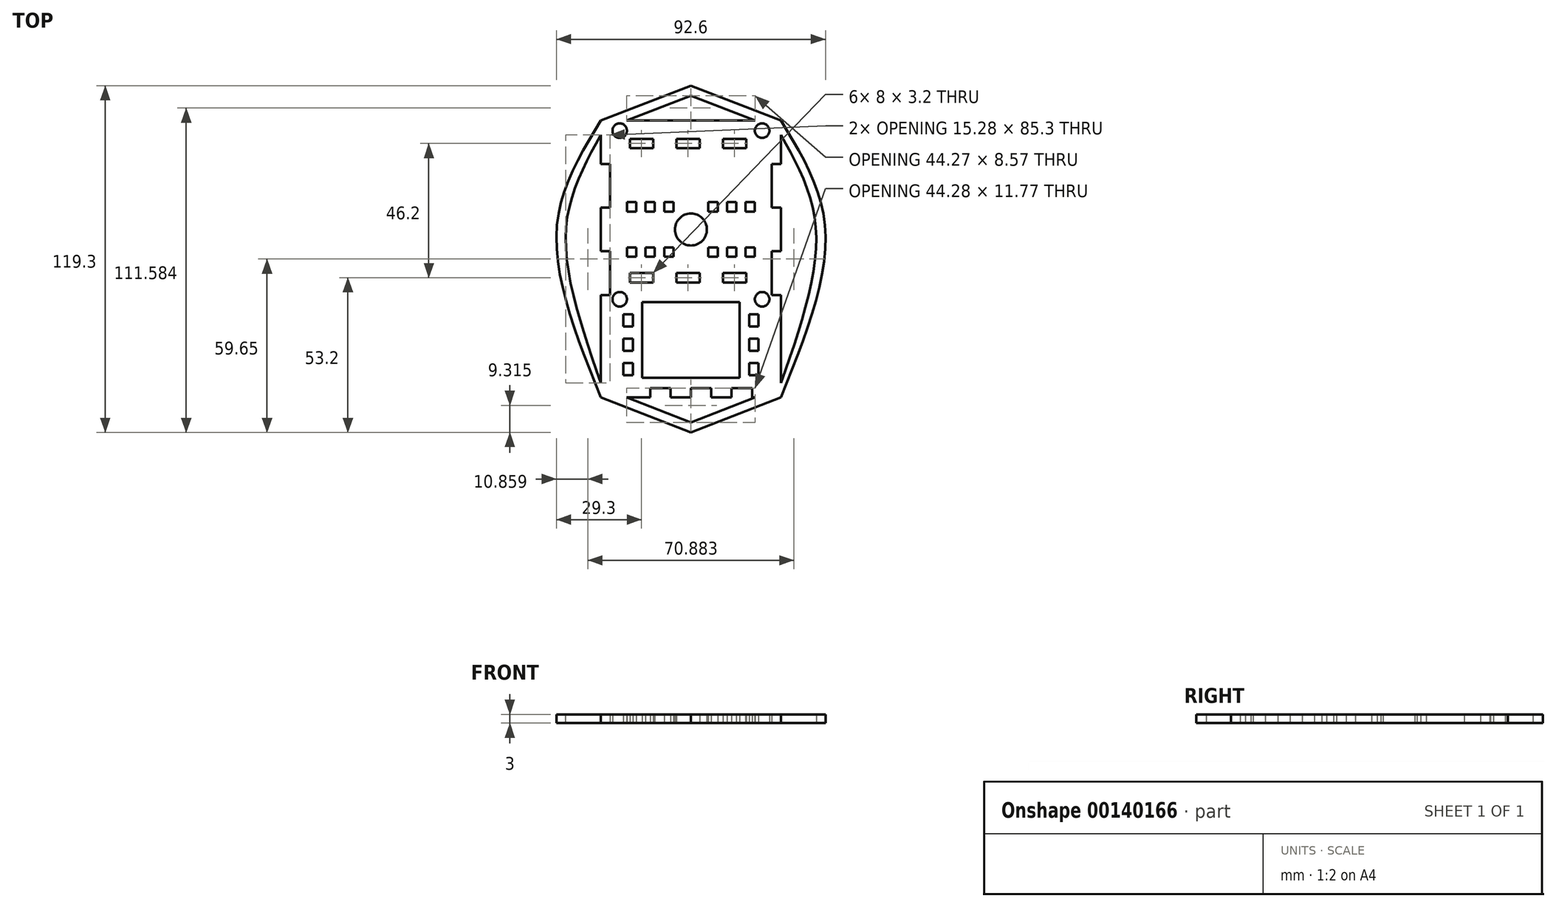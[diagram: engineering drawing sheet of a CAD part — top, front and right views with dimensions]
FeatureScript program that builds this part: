
annotation { "Feature Type Name" : "Feature", "Feature Type Description" : "" }
export const myFeature = defineFeature(function(context is Context, id is Id, definition is map)
    precondition{}
    {
        {
            var Q0;
            Q0=qCreatedBy(makeId("Top.planeOp"),FACE);
            var sketch = newSketch(context, id + "F0", { "sketchPlane" : qUnion([Q0])});
            skLineSegment(sketch, "E0.top", {"start": v(0, 37.5) * mm, "end": v(-22.14, 37.5) * mm});
            skLineSegment(sketch, "E0.right", {"start": v(-31, -32.5) * mm, "end": v(-31, -22.5) * mm});
            skPoint(sketch, "E0.middle", {"position": v(0, 0) * mm});
            skLineSegment(sketch, "E1", {"start": v(-31, 22.5) * mm, "end": v(-27.8, 22.5) * mm});
            skLineSegment(sketch, "E2", {"start": v(-27.8, 22.5) * mm, "end": v(-27.8, 7.5) * mm});
            skLineSegment(sketch, "E3", {"start": v(-27.8, 7.5) * mm, "end": v(-31, 7.5) * mm});
            skLineSegment(sketch, "E4", {"start": v(-31, 7.5) * mm, "end": v(-31, -7.5) * mm});
            skLineSegment(sketch, "E5", {"start": v(-31, -7.5) * mm, "end": v(-27.8, -7.5) * mm});
            skLineSegment(sketch, "E6", {"start": v(-27.8, -7.5) * mm, "end": v(-27.8, -22.5) * mm});
            skLineSegment(sketch, "E7", {"start": v(-27.8, -22.5) * mm, "end": v(-31, -22.5) * mm});
            skLineSegment(sketch, "E8", {"start": v(-31, -22.5) * mm, "end": v(-31, -32.5) * mm});
            skLineSegment(sketch, "E9", {"start": v(27.8, 22.5) * mm, "end": v(31, 22.5) * mm});
            skLineSegment(sketch, "E10", {"start": v(31, 7.5) * mm, "end": v(27.8, 7.5) * mm});
            skLineSegment(sketch, "E11", {"start": v(27.8, -7.5) * mm, "end": v(31, -7.5) * mm});
            skLineSegment(sketch, "E12", {"start": v(31, -22.5) * mm, "end": v(27.8, -22.5) * mm});
            skLineSegment(sketch, "E13.trimOffspring", {"start": v(-31, 22.5) * mm, "end": v(-31, 32.5) * mm});
            skLineSegment(sketch, "E14.trimOffspring", {"start": v(-31, -7.5) * mm, "end": v(-31, 7.5) * mm});
            skCircle(sketch, "E15", {"center": v(0, 0) * mm, "radius": 5.5 * mm});
            skLineSegment(sketch, "E16", {"start": v(0, 0) * mm, "end": v(5.5, 0) * mm, "construction": true});
            skLineSegment(sketch, "E17", {"start": v(-31, 0) * mm, "end": v(0, 0) * mm, "construction": true});
            skLineSegment(sketch, "E18", {"start": v(0, -14.47) * mm, "end": v(0, 12.75) * mm, "construction": true});
            skLineSegment(sketch, "E19", {"start": v(5.5, 0) * mm, "end": v(6, 0) * mm, "construction": true});
            skLineSegment(sketch, "E20", {"start": v(6, 0) * mm, "end": v(6, 9.4) * mm, "construction": true});
            skLineSegment(sketch, "E21.bottom", {"start": v(6, 9.4) * mm, "end": v(9.2, 9.4) * mm});
            skLineSegment(sketch, "E21.top", {"start": v(6, 6.2) * mm, "end": v(9.2, 6.2) * mm});
            skLineSegment(sketch, "E21.left", {"start": v(6, 9.4) * mm, "end": v(6, 6.2) * mm});
            skLineSegment(sketch, "E21.right", {"start": v(9.2, 9.4) * mm, "end": v(9.2, 6.2) * mm});
            skLineSegment(sketch, "E22", {"start": v(6, 0) * mm, "end": v(12.4, 0) * mm, "construction": true});
            skLineSegment(sketch, "E23", {"start": v(12.4, 0) * mm, "end": v(12.4, 9.4) * mm, "construction": true});
            skLineSegment(sketch, "E24", {"start": v(12.4, 0) * mm, "end": v(18.8, 0) * mm, "construction": true});
            skLineSegment(sketch, "E25", {"start": v(18.8, 0) * mm, "end": v(18.8, 9.4) * mm, "construction": true});
            skLineSegment(sketch, "E26", {"start": v(18.8, 0) * mm, "end": v(24, 0) * mm, "construction": true});
            skLineSegment(sketch, "E27.bottom", {"start": v(12.4, 9.4) * mm, "end": v(15.6, 9.4) * mm});
            skLineSegment(sketch, "E27.top", {"start": v(12.4, 6.2) * mm, "end": v(15.6, 6.2) * mm});
            skLineSegment(sketch, "E27.left", {"start": v(12.4, 9.4) * mm, "end": v(12.4, 6.2) * mm});
            skLineSegment(sketch, "E27.right", {"start": v(15.6, 9.4) * mm, "end": v(15.6, 6.2) * mm});
            skLineSegment(sketch, "E28.bottom", {"start": v(18.8, 9.4) * mm, "end": v(22, 9.4) * mm});
            skLineSegment(sketch, "E28.top", {"start": v(18.8, 6.2) * mm, "end": v(22, 6.2) * mm});
            skLineSegment(sketch, "E28.left", {"start": v(18.8, 9.4) * mm, "end": v(18.8, 6.2) * mm});
            skLineSegment(sketch, "E28.right", {"start": v(22, 9.4) * mm, "end": v(22, 6.2) * mm});
            skLineSegment(sketch, "E29.MirrorCS", {"start": v(-5.5, 0) * mm, "end": v(-6, 0) * mm, "construction": true});
            skLineSegment(sketch, "E30.MirrorCS", {"start": v(-6, 0) * mm, "end": v(-12.4, 0) * mm, "construction": true});
            skLineSegment(sketch, "E31.MirrorCS", {"start": v(-18.8, 0) * mm, "end": v(-24, 0) * mm, "construction": true});
            skLineSegment(sketch, "E32.MirrorCS", {"start": v(-12.4, 0) * mm, "end": v(-18.8, 0) * mm, "construction": true});
            skLineSegment(sketch, "E33", {"start": v(-31, 0) * mm, "end": v(27.8, 0) * mm, "construction": true});
            skLineSegment(sketch, "E34.MirrorCS", {"start": v(0, 0) * mm, "end": v(0, 30) * mm, "construction": true});
            skLineSegment(sketch, "E35.MirrorCS", {"start": v(6, -9.4) * mm, "end": v(9.2, -9.4) * mm});
            skLineSegment(sketch, "E36.MirrorCS", {"start": v(12.4, -9.4) * mm, "end": v(12.4, -6.2) * mm});
            skLineSegment(sketch, "E37.MirrorCS", {"start": v(18.8, -9.4) * mm, "end": v(18.8, -6.2) * mm});
            skLineSegment(sketch, "E38.MirrorCS", {"start": v(6, -9.4) * mm, "end": v(6, -6.2) * mm});
            skLineSegment(sketch, "E39.MirrorCS", {"start": v(18.8, -9.4) * mm, "end": v(22, -9.4) * mm});
            skLineSegment(sketch, "E40.MirrorCS", {"start": v(6, -6.2) * mm, "end": v(9.2, -6.2) * mm});
            skLineSegment(sketch, "E41.MirrorCS", {"start": v(12.4, 0) * mm, "end": v(12.4, -9.4) * mm, "construction": true});
            skLineSegment(sketch, "E42.MirrorCS", {"start": v(9.2, -9.4) * mm, "end": v(9.2, -6.2) * mm});
            skLineSegment(sketch, "E43.MirrorCS", {"start": v(15.6, -9.4) * mm, "end": v(15.6, -6.2) * mm});
            skLineSegment(sketch, "E44.MirrorCS", {"start": v(12.4, -6.2) * mm, "end": v(15.6, -6.2) * mm});
            skLineSegment(sketch, "E45.MirrorCS", {"start": v(12.4, -9.4) * mm, "end": v(15.6, -9.4) * mm});
            skLineSegment(sketch, "E46.MirrorCS", {"start": v(18.8, 0) * mm, "end": v(18.8, -9.4) * mm, "construction": true});
            skLineSegment(sketch, "E47.MirrorCS", {"start": v(18.8, -6.2) * mm, "end": v(22, -6.2) * mm});
            skLineSegment(sketch, "E48.MirrorCS", {"start": v(22, -9.4) * mm, "end": v(22, -6.2) * mm});
            skLineSegment(sketch, "E49.MirrorCS", {"start": v(6, 0) * mm, "end": v(6, -9.4) * mm, "construction": true});
            skLineSegment(sketch, "E50.MirrorCS", {"start": v(-9.2, 9.4) * mm, "end": v(-9.2, 6.2) * mm});
            skLineSegment(sketch, "E51.MirrorCS", {"start": v(-15.6, 9.4) * mm, "end": v(-15.6, 6.2) * mm});
            skLineSegment(sketch, "E52.MirrorCS", {"start": v(-12.4, 9.4) * mm, "end": v(-15.6, 9.4) * mm});
            skLineSegment(sketch, "E53.MirrorCS", {"start": v(-18.8, 6.2) * mm, "end": v(-22, 6.2) * mm});
            skLineSegment(sketch, "E54.MirrorCS", {"start": v(-18.8, 9.4) * mm, "end": v(-18.8, 6.2) * mm});
            skLineSegment(sketch, "E55.MirrorCS", {"start": v(-6, 9.4) * mm, "end": v(-9.2, 9.4) * mm});
            skLineSegment(sketch, "E56.MirrorCS", {"start": v(-22, 9.4) * mm, "end": v(-22, 6.2) * mm});
            skLineSegment(sketch, "E57.MirrorCS", {"start": v(-18.8, 9.4) * mm, "end": v(-22, 9.4) * mm});
            skLineSegment(sketch, "E58.MirrorCS", {"start": v(-6, 6.2) * mm, "end": v(-9.2, 6.2) * mm});
            skLineSegment(sketch, "E59.MirrorCS", {"start": v(-12.4, 9.4) * mm, "end": v(-12.4, 6.2) * mm});
            skLineSegment(sketch, "E60.MirrorCS", {"start": v(-12.4, 6.2) * mm, "end": v(-15.6, 6.2) * mm});
            skLineSegment(sketch, "E61.MirrorCS", {"start": v(-6, 9.4) * mm, "end": v(-6, 6.2) * mm});
            skLineSegment(sketch, "E62.MirrorCS", {"start": v(-18.8, -9.4) * mm, "end": v(-18.8, -6.2) * mm});
            skLineSegment(sketch, "E63.MirrorCS", {"start": v(-12.4, -9.4) * mm, "end": v(-12.4, -6.2) * mm});
            skLineSegment(sketch, "E64.MirrorCS", {"start": v(-6, -9.4) * mm, "end": v(-6, -6.2) * mm});
            skLineSegment(sketch, "E65.MirrorCS", {"start": v(-12.4, -9.4) * mm, "end": v(-15.6, -9.4) * mm});
            skLineSegment(sketch, "E66.MirrorCS", {"start": v(-18.8, -6.2) * mm, "end": v(-22, -6.2) * mm});
            skLineSegment(sketch, "E67.MirrorCS", {"start": v(-18.8, -9.4) * mm, "end": v(-22, -9.4) * mm});
            skLineSegment(sketch, "E68.MirrorCS", {"start": v(-12.4, -6.2) * mm, "end": v(-15.6, -6.2) * mm});
            skLineSegment(sketch, "E69.MirrorCS", {"start": v(-12.4, 0) * mm, "end": v(-12.4, -9.4) * mm, "construction": true});
            skLineSegment(sketch, "E70.MirrorCS", {"start": v(-18.8, 0) * mm, "end": v(-18.8, -9.4) * mm, "construction": true});
            skLineSegment(sketch, "E71.MirrorCS", {"start": v(-6, -9.4) * mm, "end": v(-9.2, -9.4) * mm});
            skLineSegment(sketch, "E72.MirrorCS", {"start": v(-6, 0) * mm, "end": v(-6, -9.4) * mm, "construction": true});
            skLineSegment(sketch, "E73.MirrorCS", {"start": v(-22, -9.4) * mm, "end": v(-22, -6.2) * mm});
            skLineSegment(sketch, "E74.MirrorCS", {"start": v(-9.2, -9.4) * mm, "end": v(-9.2, -6.2) * mm});
            skLineSegment(sketch, "E75.MirrorCS", {"start": v(-6, -6.2) * mm, "end": v(-9.2, -6.2) * mm});
            skLineSegment(sketch, "E76.MirrorCS", {"start": v(-15.6, -9.4) * mm, "end": v(-15.6, -6.2) * mm});
            skLineSegment(sketch, "E77", {"start": v(31, 32.5) * mm, "end": v(31, 22.5) * mm});
            skLineSegment(sketch, "E78", {"start": v(27.8, 22.5) * mm, "end": v(27.8, 7.5) * mm});
            skLineSegment(sketch, "E79", {"start": v(27.8, -7.5) * mm, "end": v(27.8, -22.5) * mm});
            skLineSegment(sketch, "E80.trimOffspring", {"start": v(31, -22.5) * mm, "end": v(31, -32.5) * mm});
            skLineSegment(sketch, "E81", {"start": v(31, 7.5) * mm, "end": v(31, -7.5) * mm});
            skLineSegment(sketch, "E82", {"start": v(31, 22.5) * mm, "end": v(34.2, 22.5) * mm});
            skLineSegment(sketch, "E83", {"start": v(0, 37.5) * mm, "end": v(0, 49.5) * mm, "construction": true});
            skPoint(sketch, "E83.startSnap0", {"position": v(0, 15) * mm});
            skLineSegment(sketch, "E84", {"start": v(0, 43.5) * mm, "end": v(34.2, 43.5) * mm, "construction": true});
            skLineSegment(sketch, "E85", {"start": v(0, 43.5) * mm, "end": v(-40.16, 43.5) * mm, "construction": true});
            skLineSegment(sketch, "E86", {"start": v(34.2, 37.5) * mm, "end": v(34.2, 43.5) * mm, "construction": true});
            skLineSegment(sketch, "E87", {"start": v(-31, 0) * mm, "end": v(-43, 0) * mm, "construction": true});
            skLineSegment(sketch, "E88", {"start": v(-27.8, 15) * mm, "end": v(-54.38, 15) * mm, "construction": true});
            skLineSegment(sketch, "E89", {"start": v(-27.8, -15) * mm, "end": v(-55.02, -15) * mm, "construction": true});
            skLineSegment(sketch, "E90", {"start": v(-31, 0) * mm, "end": v(-31, -20) * mm, "construction": true});
            skLineSegment(sketch, "E91", {"start": v(-31, 0) * mm, "end": v(-31, 20) * mm, "construction": true});
            skLineSegment(sketch, "E92", {"start": v(-31, 20) * mm, "end": v(-43, 20) * mm, "construction": true});
            skLineSegment(sketch, "E93", {"start": v(-43, 20) * mm, "end": v(-43, -20) * mm, "construction": true});
            skLineSegment(sketch, "E94", {"start": v(-31, -32.5) * mm, "end": v(-31, -28.4) * mm, "construction": true});
            skLineSegment(sketch, "E95", {"start": v(-31, 37.5) * mm, "end": v(0, 49.5) * mm});
            skLineSegment(sketch, "E96", {"start": v(0, 49.5) * mm, "end": v(31, 37.5) * mm});
            skLineSegment(sketch, "E97", {"start": v(0, 49.5) * mm, "end": v(0, 46.3) * mm, "construction": true});
            skLineSegment(sketch, "E98", {"start": v(0, 46.07) * mm, "end": v(-22.14, 37.5) * mm, "construction": true});
            skLineSegment(sketch, "E99.MirrorCS", {"start": v(0, 46.07) * mm, "end": v(22.14, 37.5) * mm, "construction": true});
            skLineSegment(sketch, "E100", {"start": v(0, 46.07) * mm, "end": v(22.14, 37.5) * mm});
            skLineSegment(sketch, "E101", {"start": v(0, 46.07) * mm, "end": v(-22.14, 37.5) * mm});
            skPoint(sketch, "E102.orphan", {"position": v(27.8, 37.5) * mm});
            skLineSegment(sketch, "E103", {"start": v(0, 37.5) * mm, "end": v(22.14, 37.5) * mm});
            skPoint(sketch, "E0.left.start.orphan", {"position": v(31, -37.5) * mm});
            skLineSegment(sketch, "E104", {"start": v(-43, 0) * mm, "end": v(-46.2, 0) * mm, "construction": true});
            skLineSegment(sketch, "E105", {"start": v(-31, 37.5) * mm, "end": v(31, 37.5) * mm, "construction": true});
            skLineSegment(sketch, "E106", {"start": v(-31, 37.5) * mm, "end": v(-31, 34.3) * mm, "construction": true});
            skLineSegment(sketch, "E107", {"start": v(-31, 34) * mm, "end": v(31, 34) * mm, "construction": true});
            skLineSegment(sketch, "E108", {"start": v(0, 34) * mm, "end": v(-24.5, 34) * mm, "construction": true});
            skLineSegment(sketch, "E109", {"start": v(-24.5, 34) * mm, "end": v(-24.5, -24) * mm, "construction": true});
            skLineSegment(sketch, "E110", {"start": v(24.5, 34) * mm, "end": v(24.5, -24) * mm, "construction": true});
            skLineSegment(sketch, "E111.MirrorCS", {"start": v(-13, 28) * mm, "end": v(-21, 28) * mm});
            skLineSegment(sketch, "E112.MirrorCS", {"start": v(-13, 28) * mm, "end": v(-5, 28) * mm, "construction": true});
            skLineSegment(sketch, "E113.MirrorCS", {"start": v(-5, 28) * mm, "end": v(-5, 31.2) * mm});
            skLineSegment(sketch, "E114.MirrorCS", {"start": v(3, 28) * mm, "end": v(-5, 28) * mm});
            skLineSegment(sketch, "E115.MirrorCS", {"start": v(3, 28) * mm, "end": v(11, 28) * mm, "construction": true});
            skLineSegment(sketch, "E116.MirrorCS", {"start": v(19, 28) * mm, "end": v(11, 28) * mm});
            skLineSegment(sketch, "E117.MirrorCS", {"start": v(-21, 28) * mm, "end": v(-21, 31.2) * mm});
            skLineSegment(sketch, "E118.MirrorCS", {"start": v(-13, 31.2) * mm, "end": v(-13, 28) * mm});
            skLineSegment(sketch, "E119.MirrorCS", {"start": v(-5, 31.2) * mm, "end": v(3, 31.2) * mm});
            skLineSegment(sketch, "E120.MirrorCS", {"start": v(3, 31.2) * mm, "end": v(3, 28) * mm});
            skLineSegment(sketch, "E121.MirrorCS", {"start": v(11, 28) * mm, "end": v(11, 31.2) * mm});
            skLineSegment(sketch, "E122.MirrorCS", {"start": v(19, 31.2) * mm, "end": v(19, 28) * mm});
            skLineSegment(sketch, "E123.MirrorCS", {"start": v(11, 31.2) * mm, "end": v(19, 31.2) * mm});
            skLineSegment(sketch, "E124.MirrorCS", {"start": v(0, 28) * mm, "end": v(21, 28) * mm, "construction": true});
            skLineSegment(sketch, "E125.MirrorCS", {"start": v(0, 28) * mm, "end": v(-21, 28) * mm, "construction": true});
            skLineSegment(sketch, "E126.MirrorCS", {"start": v(-21, 31.2) * mm, "end": v(-13, 31.2) * mm});
            skLineSegment(sketch, "E127.trimOffspring", {"start": v(-31, 32.5) * mm, "end": v(-31, 22.5) * mm});
            skLineSegment(sketch, "E128", {"start": v(43, 0) * mm, "end": v(46.2, 0) * mm, "construction": true});
            skLineSegment(sketch, "E129", {"start": v(-27.8, -15) * mm, "end": v(27.8, -15) * mm, "construction": true});
            skLineSegment(sketch, "E130", {"start": v(0, -23.1) * mm, "end": v(-21.89, -23.1) * mm, "construction": true});
            skLineSegment(sketch, "E131", {"start": v(0, -23.1) * mm, "end": v(22.57, -23.1) * mm, "construction": true});
            skLineSegment(sketch, "E132.MirrorCS", {"start": v(-13, -18.2) * mm, "end": v(-21, -18.2) * mm});
            skLineSegment(sketch, "E133.MirrorCS", {"start": v(-21, -18.2) * mm, "end": v(-21, -15) * mm});
            skLineSegment(sketch, "E134.MirrorCS", {"start": v(-21, -15) * mm, "end": v(-13, -15) * mm});
            skLineSegment(sketch, "E135.MirrorCS", {"start": v(-13, -15) * mm, "end": v(-13, -18.2) * mm});
            skLineSegment(sketch, "E136.MirrorCS", {"start": v(-13, -18.2) * mm, "end": v(-5, -18.2) * mm, "construction": true});
            skLineSegment(sketch, "E137.MirrorCS", {"start": v(-5, -18.2) * mm, "end": v(-5, -15) * mm});
            skLineSegment(sketch, "E138.MirrorCS", {"start": v(-5, -15) * mm, "end": v(3, -15) * mm});
            skLineSegment(sketch, "E139.MirrorCS", {"start": v(3, -15) * mm, "end": v(3, -18.2) * mm});
            skLineSegment(sketch, "E140.MirrorCS", {"start": v(3, -18.2) * mm, "end": v(-5, -18.2) * mm});
            skLineSegment(sketch, "E141.MirrorCS", {"start": v(0, -18.2) * mm, "end": v(-21, -18.2) * mm, "construction": true});
            skLineSegment(sketch, "E142.MirrorCS", {"start": v(11, -18.2) * mm, "end": v(11, -15) * mm});
            skLineSegment(sketch, "E143.MirrorCS", {"start": v(19, -18.2) * mm, "end": v(11, -18.2) * mm});
            skLineSegment(sketch, "E144.MirrorCS", {"start": v(19, -15) * mm, "end": v(19, -18.2) * mm});
            skLineSegment(sketch, "E145.MirrorCS", {"start": v(11, -15) * mm, "end": v(19, -15) * mm});
            skCircle(sketch, "E146", {"center": v(24.5, -24) * mm, "radius": 2.5 * mm});
            skCircle(sketch, "E147", {"center": v(-24.5, -24) * mm, "radius": 2.5 * mm});
            skCircle(sketch, "E148", {"center": v(-24.5, 34) * mm, "radius": 2.5 * mm});
            skCircle(sketch, "E149", {"center": v(24.5, 34) * mm, "radius": 2.5 * mm});
            skLineSegment(sketch, "E150", {"start": v(-31, -28.4) * mm, "end": v(31, -28.4) * mm, "construction": true});
            skLineSegment(sketch, "E151", {"start": v(0, -28.4) * mm, "end": v(0, -57.8) * mm, "construction": true});
            skLineSegment(sketch, "E152", {"start": v(0, -28.4) * mm, "end": v(-25, -28.4) * mm, "construction": true});
            skLineSegment(sketch, "E153", {"start": v(-25, -28.4) * mm, "end": v(-25, -57.8) * mm, "construction": true});
            skLineSegment(sketch, "E154", {"start": v(0, -28.4) * mm, "end": v(25, -28.4) * mm, "construction": true});
            skLineSegment(sketch, "E155", {"start": v(25, -28.4) * mm, "end": v(25, -57.8) * mm, "construction": true});
            skLineSegment(sketch, "E156", {"start": v(22.14, -57.8) * mm, "end": v(21, -57.8) * mm, "construction": true});
            skLineSegment(sketch, "E157", {"start": v(25, -28.4) * mm, "end": v(20, -28.4) * mm, "construction": true});
            skLineSegment(sketch, "E158", {"start": v(20, -28.4) * mm, "end": v(20, -57.8) * mm, "construction": true});
            skLineSegment(sketch, "E159", {"start": v(20, -28.4) * mm, "end": v(20, -29.13) * mm, "construction": true});
            skLineSegment(sketch, "E160", {"start": v(20, -29.13) * mm, "end": v(23.2, -29.13) * mm});
            skLineSegment(sketch, "E161", {"start": v(23.2, -29.13) * mm, "end": v(23.2, -33.33) * mm});
            skLineSegment(sketch, "E162", {"start": v(23.2, -33.33) * mm, "end": v(20, -33.33) * mm});
            skLineSegment(sketch, "E163", {"start": v(20, -33.33) * mm, "end": v(20, -29.13) * mm});
            skLineSegment(sketch, "E164", {"start": v(20, -33.33) * mm, "end": v(20, -37.53) * mm, "construction": true});
            skLineSegment(sketch, "E165", {"start": v(20, -37.53) * mm, "end": v(23.2, -37.53) * mm});
            skLineSegment(sketch, "E166", {"start": v(23.2, -37.53) * mm, "end": v(23.2, -41.73) * mm});
            skLineSegment(sketch, "E167", {"start": v(23.2, -41.73) * mm, "end": v(20, -41.73) * mm});
            skLineSegment(sketch, "E168", {"start": v(20, -41.73) * mm, "end": v(20, -37.53) * mm});
            skLineSegment(sketch, "E169", {"start": v(20, -41.73) * mm, "end": v(20, -45.93) * mm, "construction": true});
            skLineSegment(sketch, "E170", {"start": v(20, -45.93) * mm, "end": v(23.2, -45.93) * mm});
            skLineSegment(sketch, "E171", {"start": v(23.2, -45.93) * mm, "end": v(23.2, -50.13) * mm});
            skLineSegment(sketch, "E172", {"start": v(23.2, -50.13) * mm, "end": v(20, -50.13) * mm});
            skLineSegment(sketch, "E173", {"start": v(20, -50.13) * mm, "end": v(20, -45.93) * mm});
            skLineSegment(sketch, "E174.MirrorCS", {"start": v(-20, -28.4) * mm, "end": v(-20, -29.13) * mm, "construction": true});
            skLineSegment(sketch, "E175.MirrorCS", {"start": v(-20, -33.33) * mm, "end": v(-20, -29.13) * mm});
            skLineSegment(sketch, "E176.MirrorCS", {"start": v(-23.2, -29.13) * mm, "end": v(-23.2, -33.33) * mm});
            skLineSegment(sketch, "E177.MirrorCS", {"start": v(-20, -29.13) * mm, "end": v(-23.2, -29.13) * mm});
            skLineSegment(sketch, "E178.MirrorCS", {"start": v(-23.2, -50.13) * mm, "end": v(-20, -50.13) * mm});
            skLineSegment(sketch, "E179.MirrorCS", {"start": v(-20, -50.13) * mm, "end": v(-20, -45.93) * mm});
            skLineSegment(sketch, "E180.MirrorCS", {"start": v(-23.2, -45.93) * mm, "end": v(-23.2, -50.13) * mm});
            skLineSegment(sketch, "E181.MirrorCS", {"start": v(-20, -45.93) * mm, "end": v(-23.2, -45.93) * mm});
            skLineSegment(sketch, "E182.MirrorCS", {"start": v(-20, -41.73) * mm, "end": v(-20, -45.93) * mm, "construction": true});
            skLineSegment(sketch, "E183.MirrorCS", {"start": v(-20, -41.73) * mm, "end": v(-20, -37.53) * mm});
            skLineSegment(sketch, "E184.MirrorCS", {"start": v(-23.2, -41.73) * mm, "end": v(-20, -41.73) * mm});
            skLineSegment(sketch, "E185.MirrorCS", {"start": v(-23.2, -37.53) * mm, "end": v(-23.2, -41.73) * mm});
            skLineSegment(sketch, "E186.MirrorCS", {"start": v(-20, -37.53) * mm, "end": v(-23.2, -37.53) * mm});
            skLineSegment(sketch, "E187.MirrorCS", {"start": v(-20, -33.33) * mm, "end": v(-20, -37.53) * mm, "construction": true});
            skLineSegment(sketch, "E188.MirrorCS", {"start": v(-23.2, -33.33) * mm, "end": v(-20, -33.33) * mm});
            skLineSegment(sketch, "E189", {"start": v(-31, -32.5) * mm, "end": v(-31, -52.8) * mm});
            skLineSegment(sketch, "E190", {"start": v(-22.14, -57.8) * mm, "end": v(-14, -57.8) * mm});
            skLineSegment(sketch, "E191", {"start": v(31, -57.8) * mm, "end": v(31, -32.5) * mm});
            skFitSpline(sketch, "E192", {"points": [v(-31, 37.5) * mm, v(-46.2, 0) * mm, v(-31, -57.8) * mm], "startDerivative": vector(-47.53, -78.05) * mm, "endDerivative": vector(44.54, -111.47) * mm});
            skFitSpline(sketch, "E193", {"points": [v(-31, 32.5) * mm, v(-43, 0) * mm, v(-31, -52.8) * mm], "startDerivative": vector(-37.8, -68.26) * mm, "endDerivative": vector(35.1, -101.12) * mm});
            skLineSegment(sketch, "E194", {"start": v(0, -57.8) * mm, "end": v(0, -69.8) * mm, "construction": true});
            skLineSegment(sketch, "E195", {"start": v(0, -69.8) * mm, "end": v(0, -66.37) * mm, "construction": true});
            skLineSegment(sketch, "E196", {"start": v(-22.14, -57.8) * mm, "end": v(0, -66.37) * mm});
            skLineSegment(sketch, "E197", {"start": v(0, -66.37) * mm, "end": v(22.14, -57.8) * mm});
            skLineSegment(sketch, "E198", {"start": v(-31, -57.8) * mm, "end": v(0, -69.8) * mm});
            skLineSegment(sketch, "E199", {"start": v(0, -69.8) * mm, "end": v(31, -57.8) * mm});
            skLineSegment(sketch, "E200", {"start": v(-31, -52.8) * mm, "end": v(31, -52.8) * mm, "construction": true});
            skFitSpline(sketch, "E201", {"points": [v(31, 32.5) * mm, v(43, 0) * mm, v(31, -52.8) * mm], "startDerivative": vector(37.8, -68.26) * mm, "endDerivative": vector(-35.1, -101.12) * mm});
            skFitSpline(sketch, "E202", {"points": [v(31, 37.5) * mm, v(46.2, 0) * mm, v(31, -57.8) * mm], "startDerivative": vector(47.53, -78.05) * mm, "endDerivative": vector(-44.54, -111.47) * mm});
            skLineSegment(sketch, "E203", {"start": v(0, -23.1) * mm, "end": v(0, -52.8) * mm, "construction": true});
            skLineSegment(sketch, "E204.bottom", {"start": v(16.8, -24.92) * mm, "end": v(-16.8, -24.92) * mm});
            skLineSegment(sketch, "E204.top", {"start": v(16.8, -50.98) * mm, "end": v(-16.8, -50.98) * mm});
            skLineSegment(sketch, "E204.left", {"start": v(16.8, -24.92) * mm, "end": v(16.8, -50.98) * mm});
            skLineSegment(sketch, "E204.right", {"start": v(-16.8, -24.92) * mm, "end": v(-16.8, -50.98) * mm});
            skPoint(sketch, "E204.middle", {"position": v(0, -37.95) * mm});
            skLineSegment(sketch, "E205", {"start": v(-22.14, -57.8) * mm, "end": v(-14, -57.8) * mm, "construction": true});
            skLineSegment(sketch, "E206", {"start": v(-7, -57.8) * mm, "end": v(0, -57.8) * mm, "construction": true});
            skLineSegment(sketch, "E207", {"start": v(7, -57.8) * mm, "end": v(14, -57.8) * mm, "construction": true});
            skLineSegment(sketch, "E208", {"start": v(-14, -57.8) * mm, "end": v(-14, -54.6) * mm});
            skLineSegment(sketch, "E209", {"start": v(-14, -54.6) * mm, "end": v(-7, -54.6) * mm});
            skLineSegment(sketch, "E210", {"start": v(-7, -54.6) * mm, "end": v(-7, -57.8) * mm});
            skLineSegment(sketch, "E211", {"start": v(0, -57.8) * mm, "end": v(0, -54.6) * mm});
            skLineSegment(sketch, "E212", {"start": v(0, -54.6) * mm, "end": v(7, -54.6) * mm});
            skLineSegment(sketch, "E213", {"start": v(7, -54.6) * mm, "end": v(7, -57.8) * mm});
            skLineSegment(sketch, "E214", {"start": v(14, -57.8) * mm, "end": v(14, -54.6) * mm});
            skLineSegment(sketch, "E215", {"start": v(14, -54.6) * mm, "end": v(21, -54.6) * mm});
            skLineSegment(sketch, "E216", {"start": v(21, -54.6) * mm, "end": v(21, -57.8) * mm});
            skLineSegment(sketch, "E217.trimOffspring", {"start": v(-14, -57.8) * mm, "end": v(-22.14, -57.8) * mm, "construction": true});
            skLineSegment(sketch, "E218.trimOffspring", {"start": v(-7, -57.8) * mm, "end": v(0, -57.8) * mm});
            skLineSegment(sketch, "E219.trimOffspring", {"start": v(14, -57.8) * mm, "end": v(7, -57.8) * mm, "construction": true});
            skLineSegment(sketch, "E220.trimOffspring", {"start": v(21, -57.8) * mm, "end": v(22.14, -57.8) * mm});
            skLineSegment(sketch, "E221.trimOffspring", {"start": v(0, -57.8) * mm, "end": v(-7, -57.8) * mm, "construction": true});
            skLineSegment(sketch, "E222.trimOffspring", {"start": v(7, -57.8) * mm, "end": v(14, -57.8) * mm});
            skSolve(sketch);
        }
        {
            var Q0;
            Q0=qSketchRegion(id+"F0",true);
            extrude(context, id + "F1", {"entities" : qUnion([Q0]), "endBound" : BoundingType.SYMMETRIC, "depth" : 3 * mm});
        }
    });
